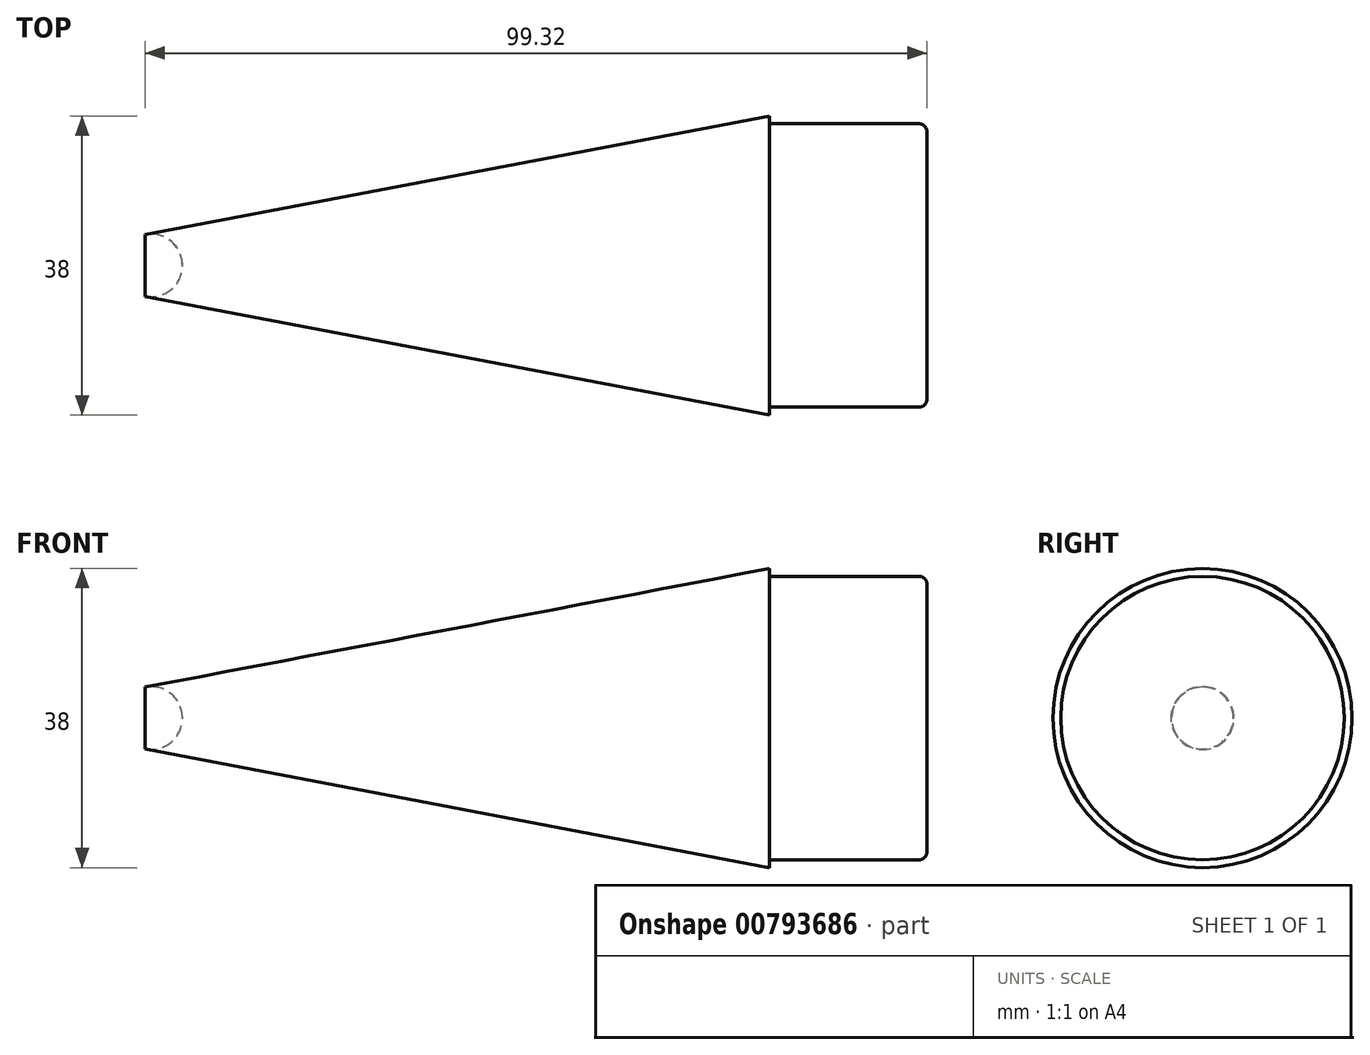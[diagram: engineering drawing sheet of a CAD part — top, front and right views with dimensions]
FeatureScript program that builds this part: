
annotation { "Feature Type Name" : "Feature", "Feature Type Description" : "" }
export const myFeature = defineFeature(function(context is Context, id is Id, definition is map)
    precondition{}
    {
        {
            var Q0;
            Q0=qCreatedBy(makeId("Top.planeOp"),FACE);
            var sketch = newSketch(context, id + "F0", { "sketchPlane" : qUnion([Q0])});
            skLineSegment(sketch, "E0", {"start": v(100, 0) * mm, "end": v(-49.92, 0) * mm, "construction": true});
            skLineSegment(sketch, "E1", {"start": v(0, 0) * mm, "end": v(0, 19) * mm, "construction": true});
            skLineSegment(sketch, "E2", {"start": v(100, 0) * mm, "end": v(100, 19) * mm, "construction": true});
            skLineSegment(sketch, "E3", {"start": v(-37.94, 19) * mm, "end": v(100, 19) * mm, "construction": true});
            skLineSegment(sketch, "E4.bottom", {"start": v(100, 18) * mm, "end": v(119, 18) * mm});
            skLineSegment(sketch, "E4.right", {"start": v(120, 17) * mm, "end": v(120, 0) * mm});
            skLineSegment(sketch, "E5", {"start": v(100, 19) * mm, "end": v(100, 18) * mm});
            skLineSegment(sketch, "E6", {"start": v(0, 0) * mm, "end": v(120, 0) * mm});
            skLineSegment(sketch, "E7.left", {"start": v(100, 19) * mm, "end": v(100, 19) * mm});
            skLineSegment(sketch, "E8.bottom", {"start": v(0, 0) * mm, "end": v(115, 0) * mm});
            skLineSegment(sketch, "E8.left", {"start": v(0, 0) * mm, "end": v(0, 14.5) * mm});
            skPoint(sketch, "E9.visualSharp", {"position": v(120, 18) * mm});
            skArc(sketch, "E9.filletArc", {"start": v(120, 17) * mm, "mid": v(119.7, 17.7) * mm, "end": v(119, 18) * mm});
            skSolve(sketch);
        }
        {
            var Q0;
            Q0=qCreatedBy(makeId("Top.planeOp"),FACE);
            var sketch = newSketch(context, id + "F1", { "sketchPlane" : qUnion([Q0])});
            skLineSegment(sketch, "E10.0", {"start": v(100, 0) * mm, "end": v(-49.92, 0) * mm});
            skLineSegment(sketch, "E10.1", {"start": v(0, 0) * mm, "end": v(0, 19) * mm});
            skLineSegment(sketch, "E10.2", {"start": v(100, 0) * mm, "end": v(100, 19) * mm});
            skLineSegment(sketch, "E10.4", {"start": v(100, 18) * mm, "end": v(119, 18) * mm});
            skLineSegment(sketch, "E10.5", {"start": v(120, 17) * mm, "end": v(120, 0) * mm});
            skLineSegment(sketch, "E10.6", {"start": v(100, 19) * mm, "end": v(100, 18) * mm});
            skLineSegment(sketch, "E10.7", {"start": v(0, 0) * mm, "end": v(120, 0) * mm});
            skPoint(sketch, "E10.8", {"position": v(100, 19) * mm});
            skLineSegment(sketch, "E10.9", {"start": v(0, 0) * mm, "end": v(115, 0) * mm});
            skLineSegment(sketch, "E10.10", {"start": v(0, 0) * mm, "end": v(0, 14.5) * mm});
            skPoint(sketch, "E11.11", {"position": v(120, 18) * mm});
            skArc(sketch, "E11.12", {"start": v(120, 17) * mm, "mid": v(119.7, 17.7) * mm, "end": v(119, 18) * mm});
            skLineSegment(sketch, "E12", {"start": v(0, 0) * mm, "end": v(100, 19) * mm});
            skCircle(sketch, "E13", {"center": v(21.43, 0) * mm, "radius": 4 * mm});
            skSolve(sketch);
        }
        {
            var Q0;
            {var subQ1=sQuery(id+"F1.wireOp",EDGE,"E10.2");Q0=makeQuery(id+"F1.imprint","IMPRINT",FACE,{"disambiguationData":[TD([[makeQuery(id+"F1.imprint","IMPRINT",EDGE,{"derivedFrom":subQ1}),1.0]])]});}
            var Q1;
            {var subQ0=sQuery(id+"F1.wireOp",EDGE,"E13");var subQ1=sQuery(id+"F1.wireOp",EDGE,"E10.9");var subQ2=makeQuery(id+"F1.imprint","INTERSECT",VERTEX,{"disambiguationData":[OD(0.0)],"derivedFrom":[subQ1,subQ0]});Q1=makeQuery(id+"F1.imprint","IMPRINT",FACE,{"disambiguationData":[TD([[makeQuery(id+"F1.imprint","IMPRINT",EDGE,{"disambiguationData":[TD([[subQ2,-1.0]])],"derivedFrom":subQ1}),1.0]])]});}
            var Q2;
            {var subQ1=sQuery(id+"F1.wireOp",EDGE,"E10.2");Q2=makeQuery(id+"F1.imprint","IMPRINT",FACE,{"disambiguationData":[TD([[makeQuery(id+"F1.imprint","IMPRINT",EDGE,{"derivedFrom":subQ1}),-1.0]])]});}
            var Q3;
            Q3=sQuery(id+"F1.wireOp",EDGE,"E10.9");
            revolve(context, id + "F2", {"surfaceOperationType" : NewSurfaceOperationType.NEW, "entities" : qUnion([Q0, Q1, Q2]), "axis" : qUnion([Q3]), "revolveType" : RevolveType.FULL});
        }
    });
